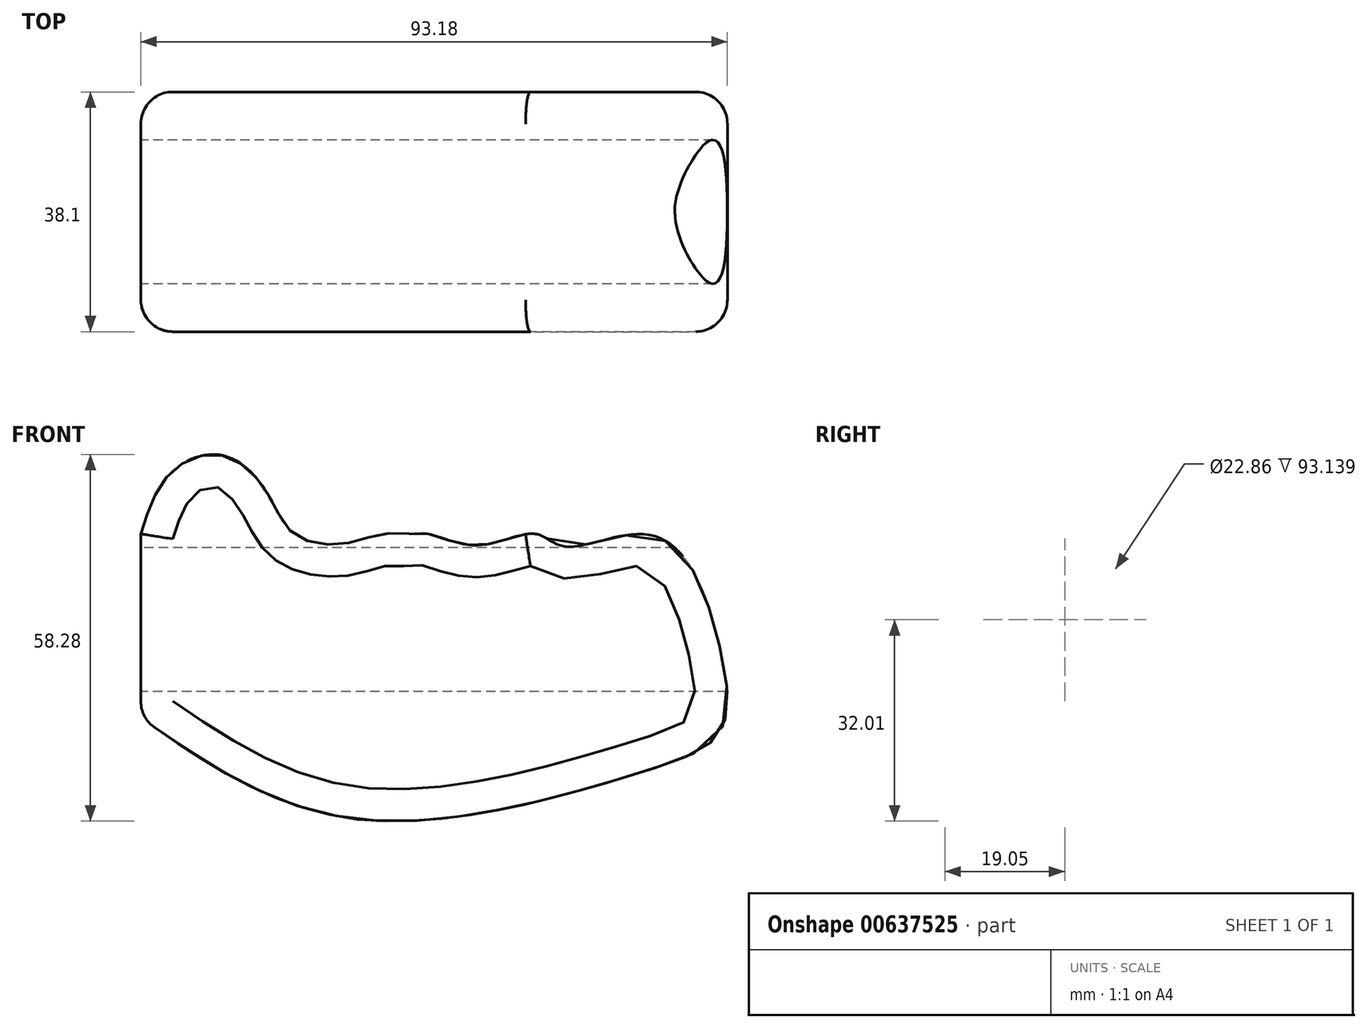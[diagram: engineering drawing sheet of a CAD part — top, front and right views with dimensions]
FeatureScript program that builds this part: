
annotation { "Feature Type Name" : "Feature", "Feature Type Description" : "" }
export const myFeature = defineFeature(function(context is Context, id is Id, definition is map)
    precondition{}
    {
        {
            var Q0;
            Q0=qCreatedBy(makeId("Front.planeOp"),FACE);
            var sketch = newSketch(context, id + "F0", { "sketchPlane" : qUnion([Q0])});
            skLineSegment(sketch, "E0", {"start": v(-42.1, -15.62) * mm, "end": v(-42.1, 13.63) * mm});
            skFitSpline(sketch, "E1", {"points": [v(-42.1, 13.63) * mm, v(-37.12, 23.59) * mm, v(-28.56, 25.97) * mm, v(-21.6, 19.4) * mm, v(-17.81, 13.63) * mm, v(-10.05, 12.04) * mm, v(-3.68, 13.63) * mm, v(0, 13.63) * mm, v(3.48, 13.63) * mm, v(11.44, 11.84) * mm, v(20.6, 13.63) * mm, v(25.18, 11.64) * mm, v(37.12, 13.63) * mm, v(45.08, 8.66) * mm, v(50.26, -6.07) * mm, v(50.06, -17.61) * mm, v(37.52, -24.18) * mm, v(-7.26, -31.75) * mm, v(-42.1, -15.62) * mm], "startDerivative": vector(64.85, 203.09) * mm, "endDerivative": vector(-307.7, 213.44) * mm});
            skSolve(sketch);
        }
        {
            var Q0;
            Q0 = qSketchRegion(id + "F0", true);
            extrude(context, id + "F1", {"entities" : qUnion([Q0]), "depth" : 19.05 * mm, "offsetDistance" : 25.4 * mm, "hasSecondDirection" : true, "secondDirectionOppositeDirection" : true, "secondDirectionDepth" : 19.05 * mm});
        }
        {
            var Q0;
            Q0=makeQuery(id+"F1.opExtrude","CAP_FACE",FACE,{"disambiguationData":[OSD([sQuery(id+"F0.wireOp",EDGE,"E0"),sQuery(id+"F0.wireOp",EDGE,"E1")])],"isStart":true});
            var Q1;
            Q1=makeQuery(id+"F1.opExtrude","CAP_FACE",FACE,{"disambiguationData":[OSD([sQuery(id+"F0.wireOp",EDGE,"E0"),sQuery(id+"F0.wireOp",EDGE,"E1")])],"isStart":false});
            var Q2;
            {var subQ0=sQuery(id+"F0.wireOp",EDGE,"E1");var subQ1=sQuery(id+"F0.wireOp",EDGE,"E0");Q2=makeQuery(id+"F1.opExtrude","SWEPT_EDGE",EDGE,{"disambiguationData":[OSD([subQ1,subQ0]),TDD([makeQuery(id+"F0.imprint","INTERSECT",VERTEX,{"disambiguationData":[OD(0.0)],"derivedFrom":[subQ1,subQ0]})])]});}
            fillet(context, id + "F2", {"entities" : qUnion([Q0, Q1, Q2]), "radius" : 5.08 * mm, "tangentPropagation" : true, "allowEdgeOverflow" : false});
        }
        {
            var Q0;
            Q0=makeQuery(id+"F1.opExtrude","SWEPT_FACE",FACE,{"disambiguationData":[OSD([sQuery(id+"F0.wireOp",EDGE,"E0")])]});
            var sketch = newSketch(context, id + "F3", { "sketchPlane" : qUnion([Q0])});
            skPoint(sketch, "E2", {"position": v(0, 0) * mm});
            skSolve(sketch);
        }
        {
            var Q0;
            Q0=sQuery(id+"F3.wireOp",VERTEX,"E2");
            var Q1;
            Q1=makeQuery(id+"F1.opExtrude","SWEPT_BODY",BODY,{"disambiguationData":[OSD([sQuery(id+"F0.wireOp",EDGE,"E0"),sQuery(id+"F0.wireOp",EDGE,"E1")])]});
            hole(context, id + "F4", {"style" : HoleStyle.SIMPLE, "endStyle" : HoleEndStyle.THROUGH, "holeDiameter" : 22.86 * mm, "majorDiameter" : 6.35 * mm, "isTappedThrough" : true, "tappedDepth" : 12.7 * mm, "tapClearance" : 3, "locations" : qUnion([Q0]), "scope" : qUnion([Q1])});
        }
    });
